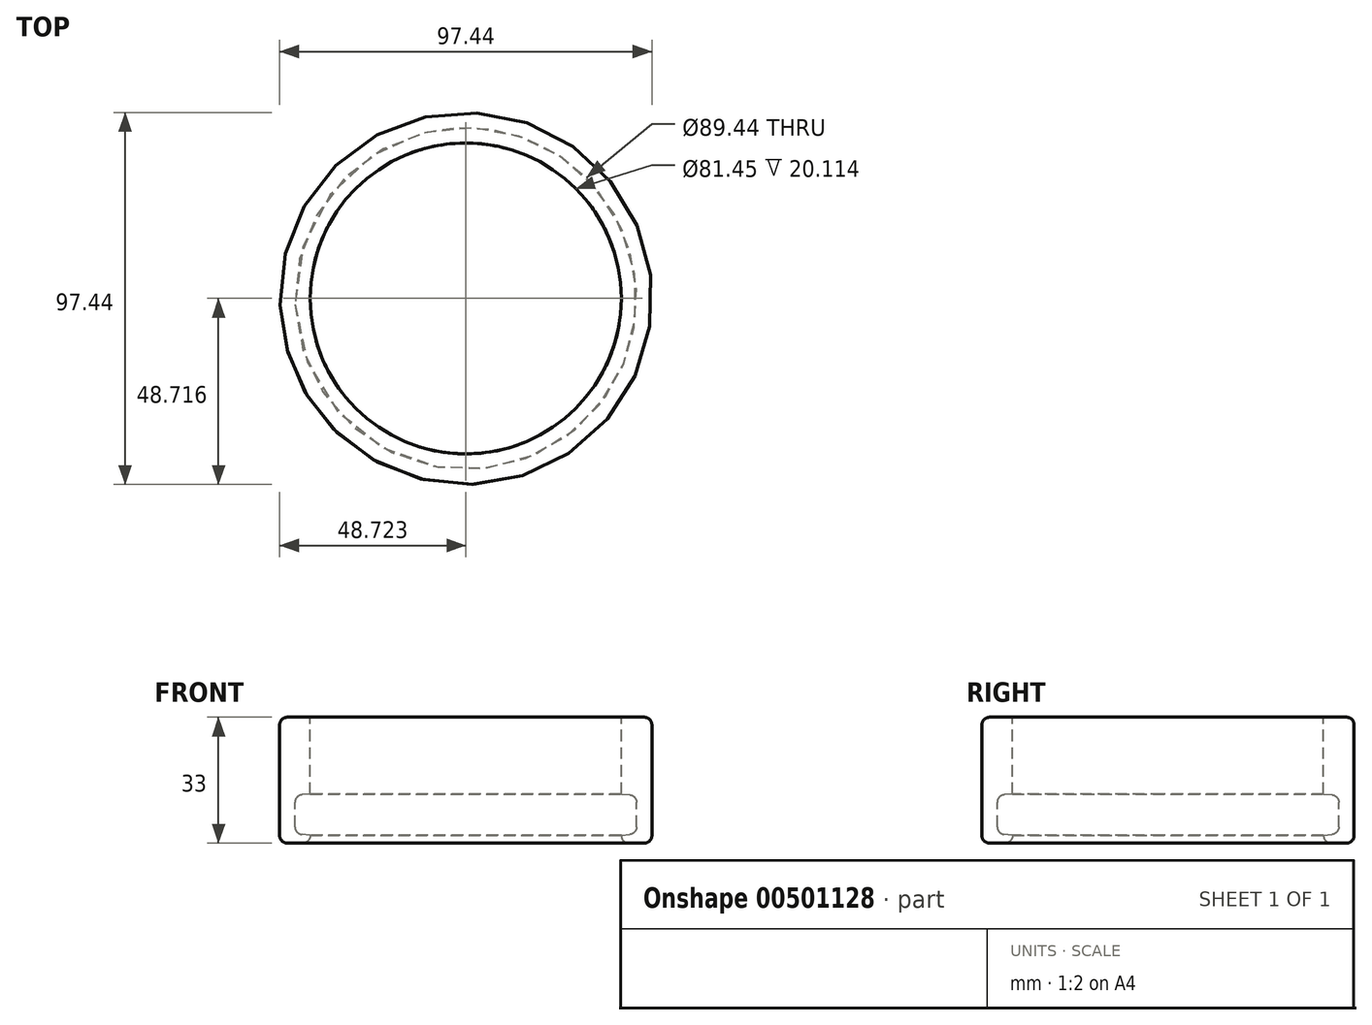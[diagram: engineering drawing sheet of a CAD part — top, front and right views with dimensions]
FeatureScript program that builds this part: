
annotation { "Feature Type Name" : "Feature", "Feature Type Description" : "" }
export const myFeature = defineFeature(function(context is Context, id is Id, definition is map)
    precondition{}
    {
        {
            var Q0;
            Q0=qCreatedBy(makeId("Front.planeOp"),FACE);
            cPlane(context, id + "F0", {"entities" : qUnion([Q0]), "cplaneType" : CPlaneType.OFFSET, "offset" : 54 * mm, "oppositeDirection" : true, "width" : 150 * mm, "height" : 150 * mm});
        }
        {
            var Q0;
            Q0=qCreatedBy(id+"F0.planeOp",FACE);
            var sketch = newSketch(context, id + "F1", { "sketchPlane" : qUnion([Q0])});
            skLineSegment(sketch, "E0.bottom", {"start": v(-2, -16.5) * mm, "end": v(2, -16.5) * mm});
            skLineSegment(sketch, "E0.top", {"start": v(-2, 16.5) * mm, "end": v(4, 16.5) * mm});
            skLineSegment(sketch, "E0.left", {"start": v(-4, -14.5) * mm, "end": v(-4, 14.5) * mm});
            skLineSegment(sketch, "E0.right", {"start": v(4, -14.5) * mm, "end": v(4, -14.5) * mm});
            skPoint(sketch, "E0.middle", {"position": v(0, 0) * mm});
            skLineSegment(sketch, "E1.bottom", {"start": v(1.8, -3.83) * mm, "end": v(4, -3.61) * mm});
            skPoint(sketch, "E1.right.end.orphan", {"position": v(15.46, 5.5) * mm});
            skPoint(sketch, "E1.right.start.orphan", {"position": v(15.53, -2.5) * mm});
            skLineSegment(sketch, "E2", {"start": v(0, 0) * mm, "end": v(0, -5.82) * mm});
            skLineSegment(sketch, "E3.trimOffspring", {"start": v(4, -3.61) * mm, "end": v(4, 16.5) * mm});
            skPoint(sketch, "E1.left.start.orphan", {"position": v(-15.46, -5.5) * mm});
            skPoint(sketch, "E4.orphan", {"position": v(-15.53, 2.5) * mm});
            skPoint(sketch, "E5.visualSharp", {"position": v(-4, 16.5) * mm});
            skArc(sketch, "E5.filletArc", {"start": v(-2, 16.5) * mm, "mid": v(-3.41, 15.91) * mm, "end": v(-4, 14.5) * mm});
            skPoint(sketch, "E6.visualSharp", {"position": v(-4, -16.5) * mm});
            skArc(sketch, "E6.filletArc", {"start": v(-4, -14.5) * mm, "mid": v(-3.41, -15.91) * mm, "end": v(-2, -16.5) * mm});
            skPoint(sketch, "E7.visualSharp", {"position": v(4, -16.5) * mm});
            skArc(sketch, "E7.filletArc", {"start": v(2, -16.5) * mm, "mid": v(3.41, -15.91) * mm, "end": v(4, -14.5) * mm});
            skLineSegment(sketch, "E8", {"start": v(1.75, -14.22) * mm, "end": v(4, -14.5) * mm});
            skLineSegment(sketch, "E9", {"start": v(0, -4) * mm, "end": v(0, -12.23) * mm});
            skPoint(sketch, "E10.visualSharp", {"position": v(0, -4) * mm});
            skArc(sketch, "E10.filletArc", {"start": v(1.8, -3.83) * mm, "mid": v(0.52, -4.47) * mm, "end": v(0, -5.82) * mm});
            skPoint(sketch, "E11.visualSharp", {"position": v(0, -14) * mm});
            skArc(sketch, "E11.filletArc", {"start": v(0, -12.23) * mm, "mid": v(0.5, -13.56) * mm, "end": v(1.75, -14.22) * mm});
            skSolve(sketch);
        }
        {
            var Q0;
            Q0=qCreatedBy(makeId("Top.planeOp"),FACE);
            var sketch = newSketch(context, id + "F2", { "sketchPlane" : qUnion([Q0])});
            skCircle(sketch, "E12", {"center": v(44.7, 55.59) * mm, "radius": 44.73 * mm});
            skPoint(sketch, "E12.first.point", {"position": v(0, 53.79) * mm});
            skPoint(sketch, "E12.second.point", {"position": v(89.42, 56.06) * mm});
            skPoint(sketch, "E12.third.point", {"position": v(60.35, 97.49) * mm});
            skSolve(sketch);
        }
        {
            var Q0;
            Q0=makeQuery(id+"F1.imprint","IMPRINT",FACE,{"disambiguationData":[TD([[makeQuery(id+"F1.imprint","IMPRINT",EDGE,{"derivedFrom":sQuery(id+"F1.wireOp",EDGE,"E0.bottom")}),1.0]])]});
            var Q1;
            Q1=sQuery(id+"F2.wireOp",EDGE,"E12");
            sweep(context, id + "F3", {"profiles" : qUnion([Q0]), "path" : qUnion([Q1])});
        }
        {
            var Q0;
            Q0=qCreatedBy(makeId("Top.planeOp"),FACE);
            var sketch = newSketch(context, id + "F4", { "sketchPlane" : qUnion([Q0])});
            skLineSegment(sketch, "E13.bottom", {"start": v(-59.3, -48.76) * mm, "end": v(-114.9, -48.76) * mm});
            skLineSegment(sketch, "E13.top", {"start": v(-59.3, 48.76) * mm, "end": v(-114.9, 48.76) * mm});
            skLineSegment(sketch, "E13.left", {"start": v(-59.3, -48.76) * mm, "end": v(-59.3, 48.76) * mm});
            skLineSegment(sketch, "E13.right", {"start": v(-114.9, -48.76) * mm, "end": v(-114.9, 48.76) * mm});
            skPoint(sketch, "E13.middle", {"position": v(-87.1, 0) * mm});
            skSolve(sketch);
        }
        {
            var Q0;
            Q0=sQuery(id+"F4.wireOp",EDGE,"E13.left");
            cPoint(context, id + "F5", {"entities" : qUnion([Q0]), "parameter" : 0.5});
        }
        {
            var Q0;
            Q0 = qCreatedBy(id + "F5" ,VERTEX);
            var Q1;
            Q1=sQuery(id+"F4.wireOp",VERTEX,"E13.middle");
            cPlane(context, id + "F6", {"entities" : qUnion([Q0, Q1]), "cplaneType" : CPlaneType.MID_PLANE, "offset" : 25 * mm, "width" : 150 * mm, "height" : 150 * mm});
        }
        {
            var Q0;
            Q0=qCreatedBy(id+"F6.planeOp",FACE);
            var sketch = newSketch(context, id + "F7", { "sketchPlane" : qUnion([Q0])});
            skCircle(sketch, "E14", {"center": v(0, 0) * mm, "radius": 10 * mm});
            skSolve(sketch);
        }
    });
